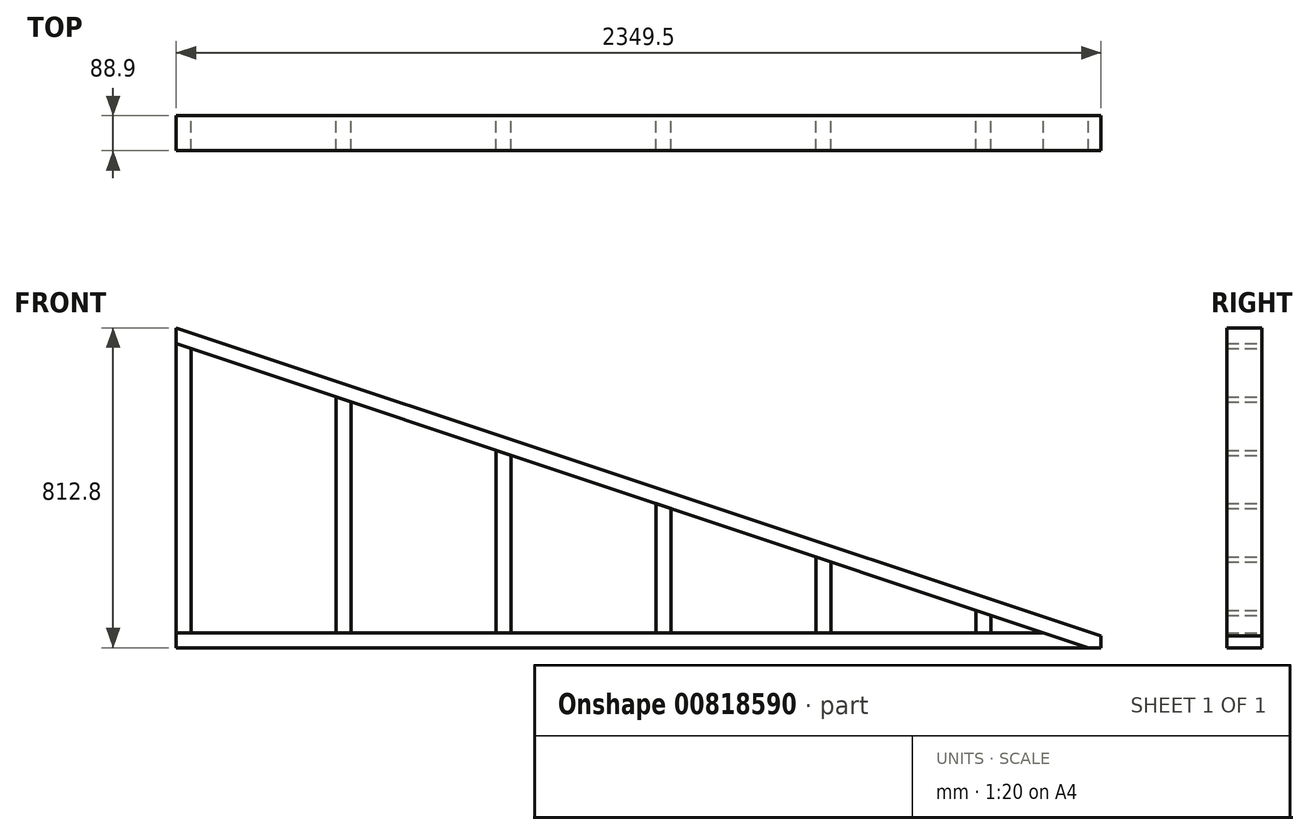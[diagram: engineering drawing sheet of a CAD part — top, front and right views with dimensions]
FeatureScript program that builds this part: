
annotation { "Feature Type Name" : "Feature", "Feature Type Description" : "" }
export const myFeature = defineFeature(function(context is Context, id is Id, definition is map)
    precondition{}
    {
        {
            var Q0;
            Q0=qCreatedBy(makeId("Front.planeOp"),FACE);
            var sketch = newSketch(context, id + "F0", { "sketchPlane" : qUnion([Q0])});
            skLineSegment(sketch, "E0.bottom", {"start": v(-1153.41, -374.87) * mm, "end": v(1196.09, -374.87) * mm});
            skLineSegment(sketch, "E0.left", {"start": v(-1153.41, -374.87) * mm, "end": v(-1153.41, 437.93) * mm});
            skLineSegment(sketch, "E1", {"start": v(-1153.41, 437.93) * mm, "end": v(1196.09, -345.24) * mm});
            skLineSegment(sketch, "E2.0", {"start": v(-1115.31, -336.77) * mm, "end": v(-1115.31, 385.07) * mm});
            skLineSegment(sketch, "E3.0", {"start": v(-1153.41, -336.77) * mm, "end": v(1050.2, -336.77) * mm});
            skLineSegment(sketch, "E4.0", {"start": v(-1153.41, 397.77) * mm, "end": v(1164.5, -374.87) * mm});
            skLineSegment(sketch, "E5.0", {"start": v(-747.01, -336.77) * mm, "end": v(-747.01, 262.3) * mm});
            skLineSegment(sketch, "E6.0", {"start": v(-708.91, -336.77) * mm, "end": v(-708.91, 249.6) * mm});
            skLineSegment(sketch, "E7.0", {"start": v(-340.61, -336.77) * mm, "end": v(-340.61, 126.83) * mm});
            skLineSegment(sketch, "E8.0", {"start": v(65.79, -336.77) * mm, "end": v(65.79, -8.63) * mm});
            skLineSegment(sketch, "E9.0", {"start": v(472.19, -336.77) * mm, "end": v(472.19, -144.1) * mm});
            skLineSegment(sketch, "E10.0", {"start": v(878.59, -336.77) * mm, "end": v(878.59, -279.57) * mm});
            skLineSegment(sketch, "E11.0", {"start": v(-302.51, -336.77) * mm, "end": v(-302.51, 114.13) * mm});
            skLineSegment(sketch, "E12.0", {"start": v(103.89, -336.77) * mm, "end": v(103.89, -21.33) * mm});
            skLineSegment(sketch, "E13.0", {"start": v(510.29, -336.77) * mm, "end": v(510.29, -156.8) * mm});
            skLineSegment(sketch, "E14.0", {"start": v(916.69, -336.77) * mm, "end": v(916.69, -292.27) * mm});
            skLineSegment(sketch, "E15", {"start": v(1284.99, -374.87) * mm, "end": v(1284.99, -250.58) * mm, "construction": true});
            skLineSegment(sketch, "E16.0", {"start": v(1196.09, -374.87) * mm, "end": v(1196.09, -345.24) * mm});
            skSolve(sketch);
        }
        {
            var Q0;
            {var subQ5=sQuery(id+"F0.wireOp",EDGE,"E2.0");Q0=makeQuery(id+"F0.imprint","IMPRINT",FACE,{"disambiguationData":[TD([[makeQuery(id+"F0.imprint","IMPRINT",EDGE,{"derivedFrom":subQ5}),1.0]])]});}
            var Q1;
            {var subQ0=sQuery(id+"F0.wireOp",EDGE,"E5.0");Q1=makeQuery(id+"F0.imprint","IMPRINT",FACE,{"disambiguationData":[TD([[makeQuery(id+"F0.imprint","IMPRINT",EDGE,{"derivedFrom":subQ0}),-1.0]])]});}
            var Q2;
            {var subQ0=sQuery(id+"F0.wireOp",EDGE,"E7.0");Q2=makeQuery(id+"F0.imprint","IMPRINT",FACE,{"disambiguationData":[TD([[makeQuery(id+"F0.imprint","IMPRINT",EDGE,{"derivedFrom":subQ0}),-1.0]])]});}
            var Q3;
            {var subQ0=sQuery(id+"F0.wireOp",EDGE,"E8.0");Q3=makeQuery(id+"F0.imprint","IMPRINT",FACE,{"disambiguationData":[TD([[makeQuery(id+"F0.imprint","IMPRINT",EDGE,{"derivedFrom":subQ0}),-1.0]])]});}
            var Q4;
            {var subQ0=sQuery(id+"F0.wireOp",EDGE,"E9.0");Q4=makeQuery(id+"F0.imprint","IMPRINT",FACE,{"disambiguationData":[TD([[makeQuery(id+"F0.imprint","IMPRINT",EDGE,{"derivedFrom":subQ0}),-1.0]])]});}
            var Q5;
            {var subQ0=sQuery(id+"F0.wireOp",EDGE,"E10.0");Q5=makeQuery(id+"F0.imprint","IMPRINT",FACE,{"disambiguationData":[TD([[makeQuery(id+"F0.imprint","IMPRINT",EDGE,{"derivedFrom":subQ0}),-1.0]])]});}
            extrude(context, id + "F1", {"entities" : qUnion([Q0, Q1, Q2, Q3, Q4, Q5]), "depth" : 88.9 * mm, "offsetDistance" : 25.4 * mm});
        }
        {
            var Q0;
            {var subQ11=sQuery(id+"F0.wireOp",EDGE,"E1");Q0=makeQuery(id+"F0.imprint","IMPRINT",FACE,{"disambiguationData":[TD([[makeQuery(id+"F0.imprint","IMPRINT",EDGE,{"derivedFrom":subQ11}),-1.0]])]});}
            extrude(context, id + "F2", {"entities" : qUnion([Q0]), "depth" : 88.9 * mm, "offsetDistance" : 25.4 * mm});
        }
        {
            var Q0;
            {var subQ8=sQuery(id+"F0.wireOp",EDGE,"E0.left");var subQ9=sQuery(id+"F0.wireOp",EDGE,"E0.bottom");var subQ10=makeQuery(id+"F0.imprint","INTERSECT",VERTEX,{"derivedFrom":[subQ9,subQ8]});Q0=makeQuery(id+"F0.imprint","IMPRINT",FACE,{"disambiguationData":[TD([[makeQuery(id+"F0.imprint","IMPRINT",EDGE,{"disambiguationData":[TD([[subQ10,-1.0]])],"derivedFrom":subQ9}),1.0]])]});}
            extrude(context, id + "F3", {"entities" : qUnion([Q0]), "depth" : 88.9 * mm, "offsetDistance" : 25.4 * mm});
        }
    });
